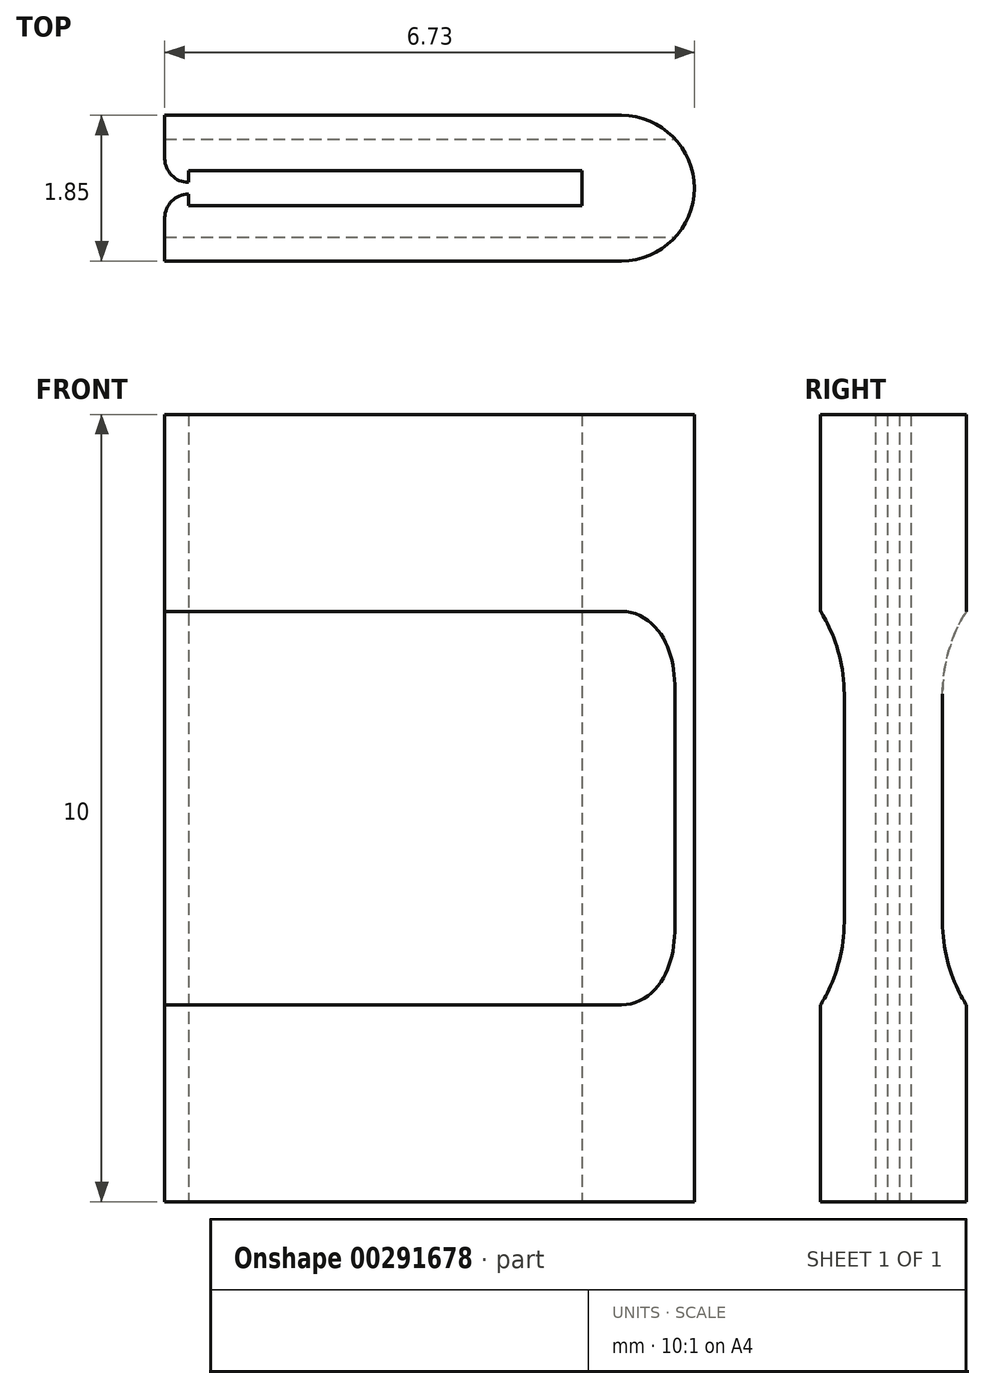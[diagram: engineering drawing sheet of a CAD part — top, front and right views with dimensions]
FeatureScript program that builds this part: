
annotation { "Feature Type Name" : "Feature", "Feature Type Description" : "" }
export const myFeature = defineFeature(function(context is Context, id is Id, definition is map)
    precondition{}
    {
        {
            var Q0;
            Q0=qCreatedBy(makeId("Top.planeOp"),FACE);
            var sketch = newSketch(context, id + "F0", { "sketchPlane" : qUnion([Q0])});
            skLineSegment(sketch, "E0", {"start": v(0, 0) * mm, "end": v(5.5, 0) * mm});
            skLineSegment(sketch, "E1", {"start": v(5.5, 1.85) * mm, "end": v(0, 1.85) * mm});
            skLineSegment(sketch, "E2", {"start": v(0, 1.15) * mm, "end": v(5, 1.15) * mm});
            skLineSegment(sketch, "E3", {"start": v(5, 1.15) * mm, "end": v(5, 0.7) * mm});
            skLineSegment(sketch, "E4", {"start": v(5, 0.7) * mm, "end": v(0, 0.7) * mm});
            skLineSegment(sketch, "E5", {"start": v(0, 0.7) * mm, "end": v(0, 0) * mm});
            skArc(sketch, "E6", {"start": v(5.5, 0) * mm, "mid": v(6.43, 0.93) * mm, "end": v(5.5, 1.85) * mm});
            skLineSegment(sketch, "E7", {"start": v(0, 1.85) * mm, "end": v(0, 1.15) * mm});
            skLineSegment(sketch, "E8.bottom", {"start": v(0, 0) * mm, "end": v(-0.3, 0) * mm});
            skLineSegment(sketch, "E8.top", {"start": v(0, 0.85) * mm, "end": v(-0.3, 0.85) * mm});
            skLineSegment(sketch, "E8.left", {"start": v(0, 0) * mm, "end": v(0, 0.85) * mm});
            skLineSegment(sketch, "E8.right", {"start": v(-0.3, 0) * mm, "end": v(-0.3, 0.85) * mm});
            skLineSegment(sketch, "E9.bottom", {"start": v(0, 1.85) * mm, "end": v(-0.3, 1.85) * mm});
            skLineSegment(sketch, "E9.top", {"start": v(0, 1) * mm, "end": v(-0.3, 1) * mm});
            skLineSegment(sketch, "E9.left", {"start": v(0, 1.85) * mm, "end": v(0, 1) * mm});
            skLineSegment(sketch, "E9.right", {"start": v(-0.3, 1.85) * mm, "end": v(-0.3, 1) * mm});
            skSolve(sketch);
        }
        {
            var Q0;
            Q0 = qSketchRegion(id + "F0", true);
            extrude(context, id + "F1", {"entities" : qUnion([Q0]), "depth" : 10 * mm});
        }
        {
            var Q0;
            Q0=makeQuery(id+"F1.opExtrude","SWEPT_EDGE",EDGE,{"disambiguationData":[OSD([sQuery(id+"F0.wireOp",EDGE,"E9.top"),sQuery(id+"F0.wireOp",EDGE,"E9.right")])]});
            var Q1;
            Q1=makeQuery(id+"F1.opExtrude","SWEPT_EDGE",EDGE,{"disambiguationData":[OSD([sQuery(id+"F0.wireOp",EDGE,"E8.top"),sQuery(id+"F0.wireOp",EDGE,"E8.right")])]});
            fillet(context, id + "F2", {"entities" : qUnion([Q0, Q1]), "radius" : .3 * mm, "tangentPropagation" : true, "allowEdgeOverflow" : false});
        }
        {
            var Q0;
            Q0=makeQuery(id+"F1.opExtrude","SWEPT_FACE",FACE,{"disambiguationData":[OSD([sQuery(id+"F0.wireOp",EDGE,"E8.right")])]});
            cPlane(context, id + "F3", {"entities" : qUnion([Q0]), "cplaneType" : CPlaneType.OFFSET, "offset" : 25 * mm, "width" : 150 * mm, "height" : 150 * mm});
        }
        {
            var Q0;
            Q0=qCreatedBy(id+"F3.planeOp",FACE);
            var sketch = newSketch(context, id + "F4", { "sketchPlane" : qUnion([Q0])});
            skLineSegment(sketch, "E10.bottom", {"start": v(0, 0) * mm, "end": v(-1.85, 0) * mm, "construction": true});
            skLineSegment(sketch, "E10.top", {"start": v(0, 10) * mm, "end": v(-1.85, 10) * mm, "construction": true});
            skLineSegment(sketch, "E10.left", {"start": v(0, 0) * mm, "end": v(0, 10) * mm, "construction": true});
            skLineSegment(sketch, "E10.right", {"start": v(-1.85, 0) * mm, "end": v(-1.85, 10) * mm, "construction": true});
            skLineSegment(sketch, "E11", {"start": v(-0.93, 10) * mm, "end": v(-0.93, 0) * mm, "construction": true});
            skLineSegment(sketch, "E12.bottom", {"start": v(-0.3, 2.5) * mm, "end": v(0.3, 2.5) * mm});
            skLineSegment(sketch, "E12.top", {"start": v(-0.3, 7.5) * mm, "end": v(0.3, 7.5) * mm});
            skLineSegment(sketch, "E12.left", {"start": v(-0.3, 2.5) * mm, "end": v(-0.3, 7.5) * mm});
            skLineSegment(sketch, "E12.right", {"start": v(0.3, 2.5) * mm, "end": v(0.3, 7.5) * mm});
            skPoint(sketch, "E12.middle", {"position": v(0, 5) * mm});
            skLineSegment(sketch, "E13.MirrorCS", {"start": v(-2.15, 2.5) * mm, "end": v(-2.15, 7.5) * mm});
            skLineSegment(sketch, "E14.MirrorCS", {"start": v(-1.55, 7.5) * mm, "end": v(-2.15, 7.5) * mm});
            skLineSegment(sketch, "E15.MirrorCS", {"start": v(-1.55, 2.5) * mm, "end": v(-1.55, 7.5) * mm});
            skLineSegment(sketch, "E16.MirrorCS", {"start": v(-1.55, 2.5) * mm, "end": v(-2.15, 2.5) * mm});
            skSolve(sketch);
        }
        {
            var Q0;
            Q0 = qSketchRegion(id + "F4", true);
            extrude(context, id + "F5", {"entities" : qUnion([Q0]), "operationType" : NewBodyOperationType.REMOVE, "oppositeDirection" : true, "depth" : 32.8 * mm});
        }
        {
            var Q0;
            Q0=makeQuery(id+"F5.boolean.opBoolean","COPY",EDGE,{"derivedFrom":makeQuery(id+"F5.opExtrude","SWEPT_EDGE",EDGE,{"disambiguationData":[OSD([sQuery(id+"F4.wireOp",EDGE,"E14.MirrorCS"),sQuery(id+"F4.wireOp",EDGE,"E15.MirrorCS")])]})});
            var Q1;
            Q1=makeQuery(id+"F5.boolean.opBoolean","COPY",EDGE,{"derivedFrom":makeQuery(id+"F5.opExtrude","SWEPT_EDGE",EDGE,{"disambiguationData":[OSD([sQuery(id+"F4.wireOp",EDGE,"E15.MirrorCS"),sQuery(id+"F4.wireOp",EDGE,"E16.MirrorCS")])]})});
            var Q2;
            Q2=makeQuery(id+"F5.boolean.opBoolean","COPY",EDGE,{"derivedFrom":makeQuery(id+"F5.opExtrude","SWEPT_EDGE",EDGE,{"disambiguationData":[OSD([sQuery(id+"F4.wireOp",EDGE,"E12.bottom"),sQuery(id+"F4.wireOp",EDGE,"E12.left")])]})});
            var Q3;
            Q3=makeQuery(id+"F5.boolean.opBoolean","COPY",EDGE,{"derivedFrom":makeQuery(id+"F5.opExtrude","SWEPT_EDGE",EDGE,{"disambiguationData":[OSD([sQuery(id+"F4.wireOp",EDGE,"E12.top"),sQuery(id+"F4.wireOp",EDGE,"E12.left")])]})});
            fillet(context, id + "F6", {"entities" : qUnion([Q0, Q1, Q2, Q3]), "radius" : 2 * mm, "tangentPropagation" : true, "allowEdgeOverflow" : false});
        }
    });
